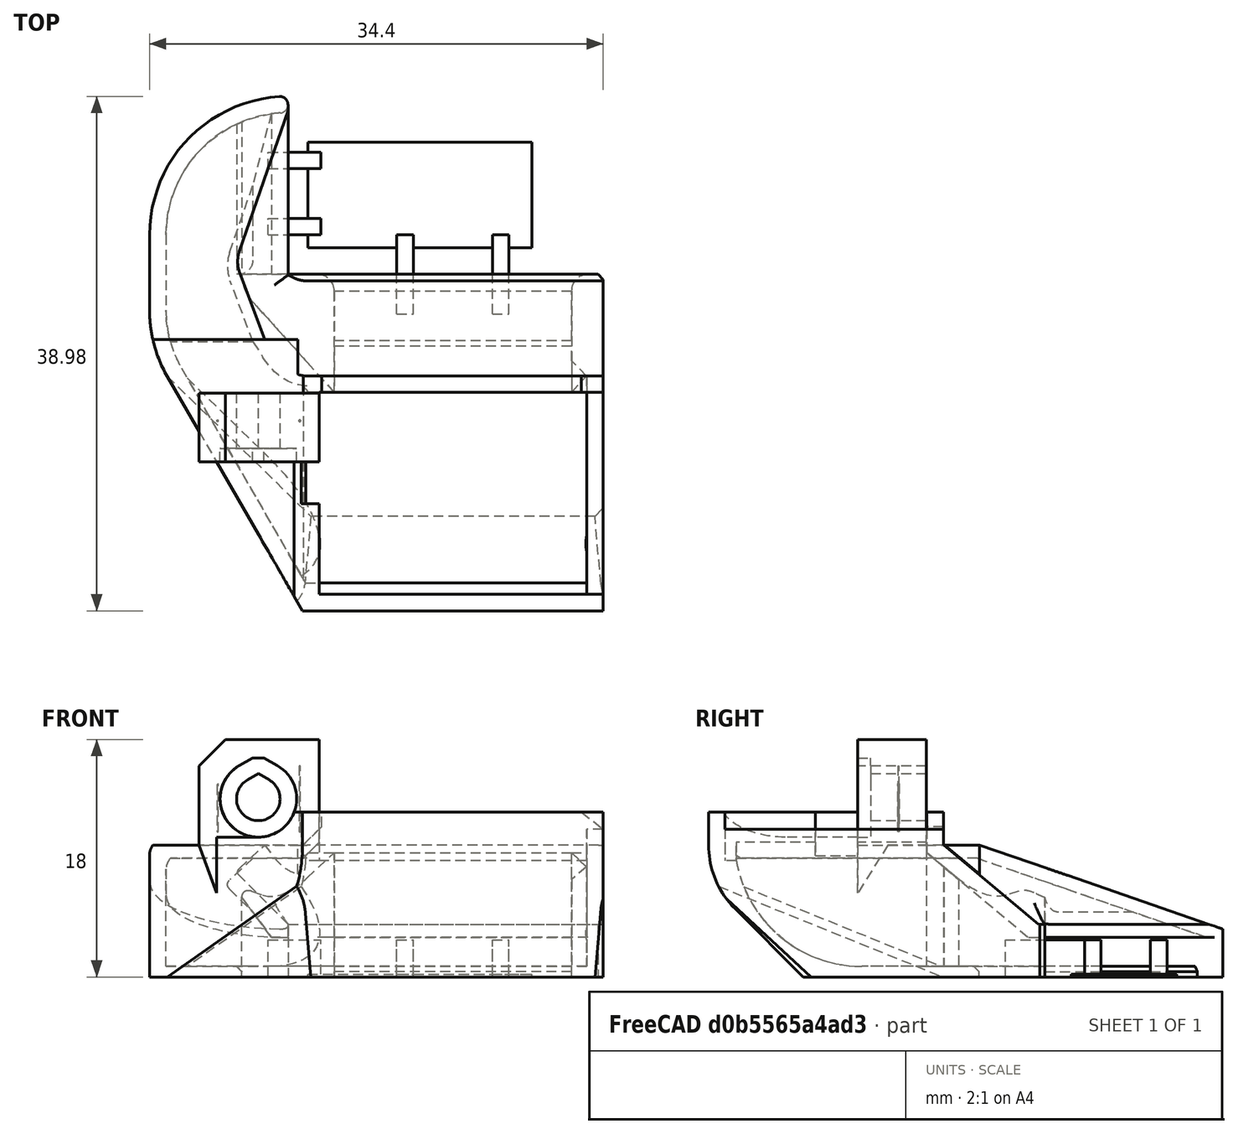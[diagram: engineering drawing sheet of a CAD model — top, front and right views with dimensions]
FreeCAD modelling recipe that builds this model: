
FCSTD DOCUMENT  (FreeCAD 0.18R16146 (Git))
Label: mosquito-duct-lite-mirror
License: All rights reserved
LicenseURL: http://en.wikipedia.org/wiki/All_rights_reserved
objects: Part::Box×8, Part::Chamfer×4, Part::Feature×3, Part::Cut×3, Part::MultiFuse×2
note: 20 computed .brp shape members not serialized (recipe doc carries the construction recipe); baked Part::Feature solids carry a one-line shape summary decoded from their .brp

FEATURE [Part::Feature] Part__Feature050  label="nozzle_fan_duct"
  Placement = pos=(0.005,14,-6.0794e-11) rot=(0,0,1;0rad)
  shape: bbox 46.01 x 38.99 x 18.01 mm, 128 faces (baked)
FEATURE [Part::Box] Box009  label="Cube009"
  AttacherType = Attacher::AttachEngine3D
  Height = 2.8
  Length = 1.25
  Placement = pos=(3,-3,0) rot=(0,0,1;0rad)
  Width = 6
FEATURE [Part::Box] Box010  label="Cube010"
  AttacherType = Attacher::AttachEngine3D
  Height = 2.8
  Length = 1.25
  Placement = pos=(-4.25,-3,0) rot=(0,0,1;0rad)
  Width = 6
FEATURE [Part::Box] Box011  label="Cube011"
  AttacherType = Attacher::AttachEngine3D
  Height = 2.8
  Length = 4
  Placement = pos=(-14,3,0) rot=(0,0,1;0rad)
  Width = 1.25
FEATURE [Part::Box] Box012  label="Cube012"
  AttacherType = Attacher::AttachEngine3D
  Height = 2.8
  Length = 4
  Placement = pos=(-14,8,0) rot=(0,0,1;0rad)
  Width = 1.25
FEATURE [Part::Box] Box013  label="Cube013"
  AttacherType = Attacher::AttachEngine3D
  Height = 0.2
  Length = 17
  Placement = pos=(-11,2,0) rot=(0,0,1;0rad)
  Width = 8
FEATURE [Part::Box] Box  label="Cube"
  AttacherType = Attacher::AttachEngine3D
  Height = 13
  Length = 14
  Placement = pos=(11.4,-27,0) rot=(0,0,1;0rad)
  Width = 44
FEATURE [Part::Cut] Cut
  Base = -> Part__Feature050
  Tool = -> Box
FEATURE [Part::Box] Box014  label="Cube014"
  AttacherType = Attacher::AttachEngine3D
  Height = 10
  Length = 1.24
  Placement = pos=(10.16,-24,0) rot=(0,0,1;0rad)
  Width = 19
FEATURE [Part::Chamfer] Chamfer002
  Base = -> Cut
  Edges = 1 edges r=0.4: [Edge69]
FEATURE [Part::MultiFuse] Fusion001  label="support"
  Shapes = -> [Box010,Box011,Box009,Box012,Box013]
FEATURE [Part::Box] Box015  label="Cube015"
  AttacherType = Attacher::AttachEngine3D
  Height = 8.61
  Length = 3
  Placement = pos=(7.15,-10.7,0.8) rot=(0,0,1;0rad)
  Width = 3
FEATURE [Part::Chamfer] Chamfer
  Base = -> Box015
  Edges = 1 edges r=1.15: [Edge7]
  Placement = pos=(0,1.15,0) rot=(0,0,1;0rad)
FEATURE [Part::Feature] Box016001  label="Cube017"
  Placement = pos=(0,0,0.1) rot=(0,0,1;0rad)
  shape: bbox 10 x 10.88 x 10.24 mm, 6 faces (baked)
FEATURE [Part::Cut] Cut001
  Base = -> Chamfer
  Tool = -> Box016001
FEATURE [Part::Cut] Cut002
  Base = -> Chamfer002
  Tool = -> Cut001
FEATURE [Part::Chamfer] Chamfer003
  Base = -> Box014
  Edges = 1 edges r=3: [Edge12]
FEATURE [Part::Chamfer] Chamfer004
  Base = -> Chamfer003
  Edges = 1 edges r=6.5: [Edge11]
FEATURE [Part::MultiFuse] Fusion  label="duct-base-r1"
  Shapes = -> [Chamfer004,Cut002]
FEATURE [Part::Feature] Fusion002  label="duct-base-r002"
  shape: bbox 34.41 x 38.99 x 18.01 mm, 108 faces (baked)
